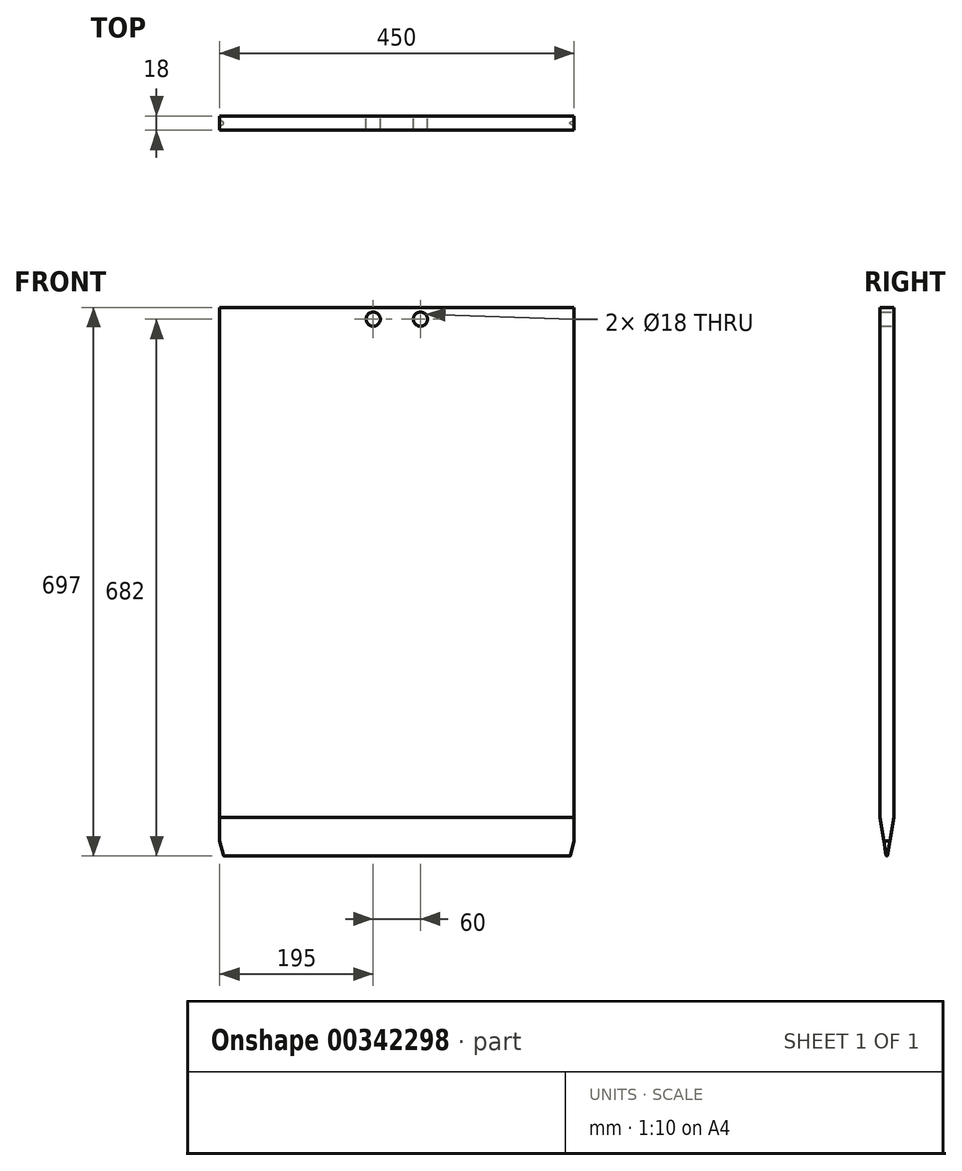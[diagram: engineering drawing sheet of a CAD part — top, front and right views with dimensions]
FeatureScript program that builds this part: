
annotation { "Feature Type Name" : "Feature", "Feature Type Description" : "" }
export const myFeature = defineFeature(function(context is Context, id is Id, definition is map)
    precondition{}
    {
        {
            var Q0;
            Q0=qCreatedBy(makeId("Right.planeOp"),FACE);
            var sketch = newSketch(context, id + "F0", { "sketchPlane" : qUnion([Q0])});
            skLineSegment(sketch, "E0.bottom", {"start": v(9, 348.5) * mm, "end": v(-9, 348.5) * mm});
            skLineSegment(sketch, "E0.top", {"start": v(9, -348.5) * mm, "end": v(-9, -348.5) * mm});
            skLineSegment(sketch, "E0.left", {"start": v(9, 348.5) * mm, "end": v(9, -348.5) * mm});
            skLineSegment(sketch, "E0.right", {"start": v(-9, 348.5) * mm, "end": v(-9, -348.5) * mm});
            skPoint(sketch, "E0.middle", {"position": v(0, 0) * mm});
            skPoint(sketch, "E1", {"position": v(0, -348.5) * mm});
            skCircle(sketch, "E2", {"center": v(0, -347.5) * mm, "radius": 1 * mm});
            skLineSegment(sketch, "E3", {"start": v(-9, -299.5) * mm, "end": v(-0.99, -347.66) * mm});
            skLineSegment(sketch, "E4", {"start": v(0.99, -347.66) * mm, "end": v(9, -299.5) * mm});
            skSolve(sketch);
        }
        {
            var Q0;
            {var subQ4=sQuery(id+"F0.wireOp",EDGE,"E0.bottom");Q0=makeQuery(id+"F0.imprint","IMPRINT",FACE,{"disambiguationData":[TD([[makeQuery(id+"F0.imprint","IMPRINT",EDGE,{"derivedFrom":subQ4}),1.0]])]});}
            var Q1;
            {var subQ0=sQuery(id+"F0.wireOp",EDGE,"E2");var subQ1=makeQuery(id+"F0.imprint","INTERSECT",VERTEX,{"derivedFrom":[subQ0,sQuery(id+"F0.wireOp",EDGE,"E3")]});Q1=makeQuery(id+"F0.imprint","IMPRINT",FACE,{"disambiguationData":[TD([[makeQuery(id+"F0.imprint","IMPRINT",EDGE,{"disambiguationData":[TD([[subQ1,-1.0]])],"derivedFrom":subQ0}),1.0]])]});}
            extrude(context, id + "F1", {"entities" : qUnion([Q0, Q1]), "endBound" : BoundingType.SYMMETRIC, "depth" : 450 * mm});
        }
        {
            var Q0;
            Q0=makeQuery(id+"F1.opExtrude","SWEPT_FACE",FACE,{"disambiguationData":[OSD([sQuery(id+"F0.wireOp",EDGE,"E0.left")])]});
            var sketch = newSketch(context, id + "F2", { "sketchPlane" : qUnion([Q0])});
            skCircle(sketch, "E5", {"center": v(30, 333.5) * mm, "radius": 9 * mm});
            skCircle(sketch, "E6", {"center": v(-30, 333.5) * mm, "radius": 9 * mm});
            skLineSegment(sketch, "E7", {"start": v(-225, -329.5) * mm, "end": v(-220.07, -348.5) * mm});
            skLineSegment(sketch, "E8", {"start": v(-225.07, -348.5) * mm, "end": v(-220.07, -348.5) * mm});
            skLineSegment(sketch, "E9", {"start": v(-225, -329.5) * mm, "end": v(-225.07, -348.5) * mm});
            skLineSegment(sketch, "E10.MirrorCS", {"start": v(225, -329.5) * mm, "end": v(220.07, -348.5) * mm});
            skLineSegment(sketch, "E11.MirrorCS", {"start": v(225, -329.5) * mm, "end": v(225.07, -348.5) * mm});
            skLineSegment(sketch, "E12.MirrorCS", {"start": v(225.07, -348.5) * mm, "end": v(220.07, -348.5) * mm});
            skLineSegment(sketch, "E13", {"start": v(30, 333.5) * mm, "end": v(225, 333.5) * mm});
            skLineSegment(sketch, "E14", {"start": v(-30, 333.5) * mm, "end": v(-225, 333.5) * mm});
            skSolve(sketch);
        }
        {
            var Q0;
            Q0=qSketchRegion(id+"F2",true);
            extrude(context, id + "F3", {"entities" : qUnion([Q0]), "operationType" : NewBodyOperationType.REMOVE, "oppositeDirection" : true, "depth" : 25 * mm});
        }
    });
